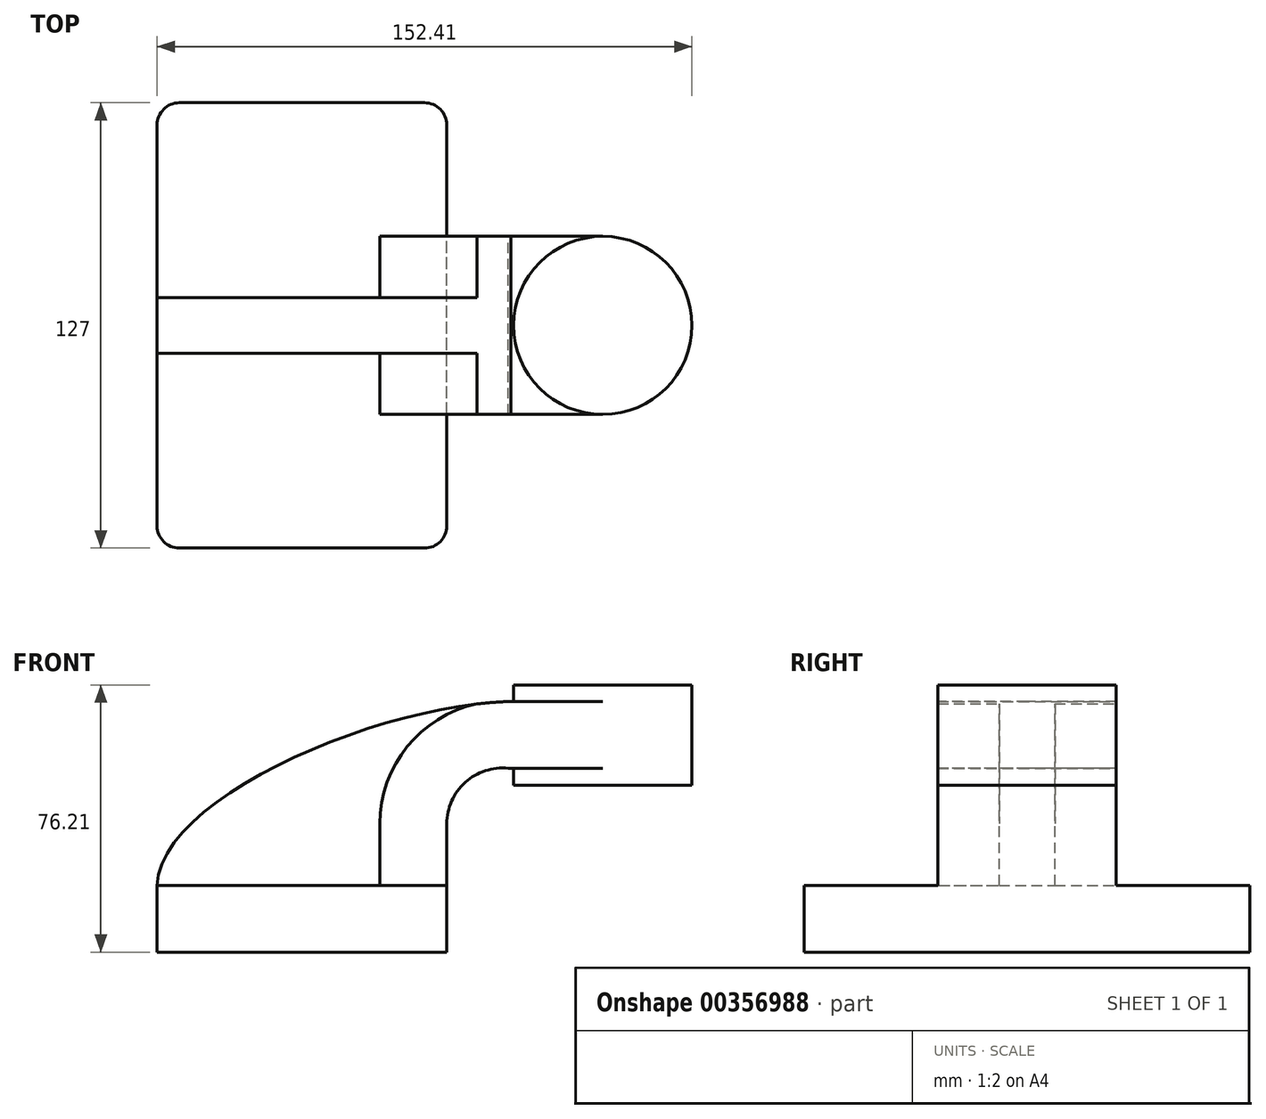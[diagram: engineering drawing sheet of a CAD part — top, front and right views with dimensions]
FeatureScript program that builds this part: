
annotation { "Feature Type Name" : "Feature", "Feature Type Description" : "" }
export const myFeature = defineFeature(function(context is Context, id is Id, definition is map)
    precondition{}
    {
        {
            var Q0;
            Q0=qCreatedBy(makeId("Front.planeOp"),FACE);
            var sketch = newSketch(context, id + "F0", { "sketchPlane" : qUnion([Q0])});
            skLineSegment(sketch, "E0.bottom", {"start": v(41.27, 9.53) * mm, "end": v(-41.28, 9.53) * mm});
            skLineSegment(sketch, "E0.top", {"start": v(41.28, -9.52) * mm, "end": v(-41.27, -9.52) * mm});
            skLineSegment(sketch, "E0.left", {"start": v(41.28, 9.53) * mm, "end": v(41.28, -9.52) * mm});
            skLineSegment(sketch, "E0.right", {"start": v(-41.28, 9.53) * mm, "end": v(-41.27, -9.52) * mm});
            skPoint(sketch, "E0.middle", {"position": v(0, 0) * mm});
            skLineSegment(sketch, "E1.bottom", {"start": v(111.12, 38.1) * mm, "end": v(60.33, 38.1) * mm});
            skLineSegment(sketch, "E1.top", {"start": v(111.13, 66.68) * mm, "end": v(60.33, 66.68) * mm});
            skLineSegment(sketch, "E1.left", {"start": v(111.13, 38.1) * mm, "end": v(111.13, 66.68) * mm});
            skLineSegment(sketch, "E1.right", {"start": v(60.33, 38.1) * mm, "end": v(60.33, 66.68) * mm});
            skPoint(sketch, "E1.middle", {"position": v(85.73, 52.39) * mm});
            skLineSegment(sketch, "E2", {"start": v(41.27, 9.53) * mm, "end": v(41.27, 27.08) * mm});
            skArc(sketch, "E3", {"start": v(41.28, 27.08) * mm, "mid": v(46.52, 38.87) * mm, "end": v(58.79, 42.88) * mm});
            skLineSegment(sketch, "E4", {"start": v(58.79, 42.88) * mm, "end": v(85.73, 42.88) * mm});
            skLineSegment(sketch, "E5.0", {"start": v(59.58, 61.93) * mm, "end": v(85.73, 61.93) * mm});
            skArc(sketch, "E5.1", {"start": v(22.23, 27.08) * mm, "mid": v(33.33, 52.62) * mm, "end": v(59.58, 61.93) * mm});
            skLineSegment(sketch, "E5.2", {"start": v(22.22, 9.53) * mm, "end": v(22.22, 27.08) * mm});
            skFitSpline(sketch, "E6", {"points": [v(-41.28, 9.53) * mm, v(59.58, 61.93) * mm], "startDerivative": vector(3, 75.93) * mm, "endDerivative": vector(111.95, 2.16) * mm});
            skLineSegment(sketch, "E7", {"start": v(85.73, 42.88) * mm, "end": v(85.73, 66.68) * mm});
            skLineSegment(sketch, "E8", {"start": v(85.72, 42.88) * mm, "end": v(85.72, 38.1) * mm});
            skSolve(sketch);
        }
        {
            var Q0;
            {var subQ1=sQuery(id+"F0.wireOp",EDGE,"E2");Q0=makeQuery(id+"F0.imprint","IMPRINT",FACE,{"disambiguationData":[TD([[makeQuery(id+"F0.imprint","IMPRINT",EDGE,{"derivedFrom":subQ1}),1.0]])]});}
            extrude(context, id + "F1", {"entities" : qUnion([Q0]), "endBound" : BoundingType.SYMMETRIC, "depth" : 50.8 * mm});
        }
        {
            var Q0;
            {var subQ3=sQuery(id+"F0.wireOp",EDGE,"E5.2");Q0=makeQuery(id+"F0.imprint","IMPRINT",FACE,{"disambiguationData":[TD([[makeQuery(id+"F0.imprint","IMPRINT",EDGE,{"derivedFrom":subQ3}),1.0]])]});}
            extrude(context, id + "F2", {"entities" : qUnion([Q0]), "operationType" : NewBodyOperationType.ADD, "endBound" : BoundingType.SYMMETRIC, "depth" : 15.88 * mm});
        }
        {
            var Q0;
            Q0=makeQuery(id+"F0.imprint","IMPRINT",FACE,{"disambiguationData":[TD([[makeQuery(id+"F0.imprint","IMPRINT",EDGE,{"derivedFrom":sQuery(id+"F0.wireOp",EDGE,"E0.top")}),-1.0]])]});
            extrude(context, id + "F3", {"entities" : qUnion([Q0]), "operationType" : NewBodyOperationType.ADD, "endBound" : BoundingType.SYMMETRIC, "depth" : 127 * mm});
        }
        {
            var Q0;
            {var subQ0=sQuery(id+"F0.wireOp",EDGE,"E4");var subQ1=sQuery(id+"F0.wireOp",EDGE,"E1.right");var subQ2=makeQuery(id+"F0.imprint","INTERSECT",VERTEX,{"derivedFrom":[subQ1,subQ0]});Q0=makeQuery(id+"F0.imprint","IMPRINT",FACE,{"disambiguationData":[TD([[makeQuery(id+"F0.imprint","IMPRINT",EDGE,{"disambiguationData":[TD([[subQ2,-1.0]])],"derivedFrom":subQ1}),-1.0]])]});}
            extrude(context, id + "F4", {"entities" : qUnion([Q0]), "operationType" : NewBodyOperationType.ADD, "endBound" : BoundingType.SYMMETRIC, "depth" : 50.8 * mm});
        }
        {
            var Q0;
            {var subQ3=sQuery(id+"F0.wireOp",EDGE,"E1.left");Q0=makeQuery(id+"F0.imprint","IMPRINT",FACE,{"disambiguationData":[TD([[makeQuery(id+"F0.imprint","IMPRINT",EDGE,{"derivedFrom":subQ3}),1.0]])]});}
            var Q1;
            Q1=sQuery(id+"F0.wireOp",EDGE,"E7");
            revolve(context, id + "F5", {"operationType" : NewBodyOperationType.ADD, "entities" : qUnion([Q0]), "axis" : qUnion([Q1]), "revolveType" : RevolveType.FULL});
        }
        {
            var Q0;
            Q0=makeQuery(id+"F3.opExtrude","CAP_EDGE",EDGE,{"disambiguationData":[OSD([sQuery(id+"F0.wireOp",EDGE,"E0.right")])],"isStart":false});
            var Q1;
            Q1=makeQuery(id+"F3.opExtrude","CAP_EDGE",EDGE,{"disambiguationData":[OSD([sQuery(id+"F0.wireOp",EDGE,"E0.left")])],"isStart":false});
            var Q2;
            Q2=makeQuery(id+"F3.opExtrude","CAP_EDGE",EDGE,{"disambiguationData":[OSD([sQuery(id+"F0.wireOp",EDGE,"E0.right")])],"isStart":true});
            var Q3;
            Q3=makeQuery(id+"F3.opExtrude","CAP_EDGE",EDGE,{"disambiguationData":[OSD([sQuery(id+"F0.wireOp",EDGE,"E0.left")])],"isStart":true});
            fillet(context, id + "F6", {"entities" : qUnion([Q0, Q1, Q2, Q3]), "radius" : 6.35 * mm, "tangentPropagation" : true, "allowEdgeOverflow" : false});
        }
    });
